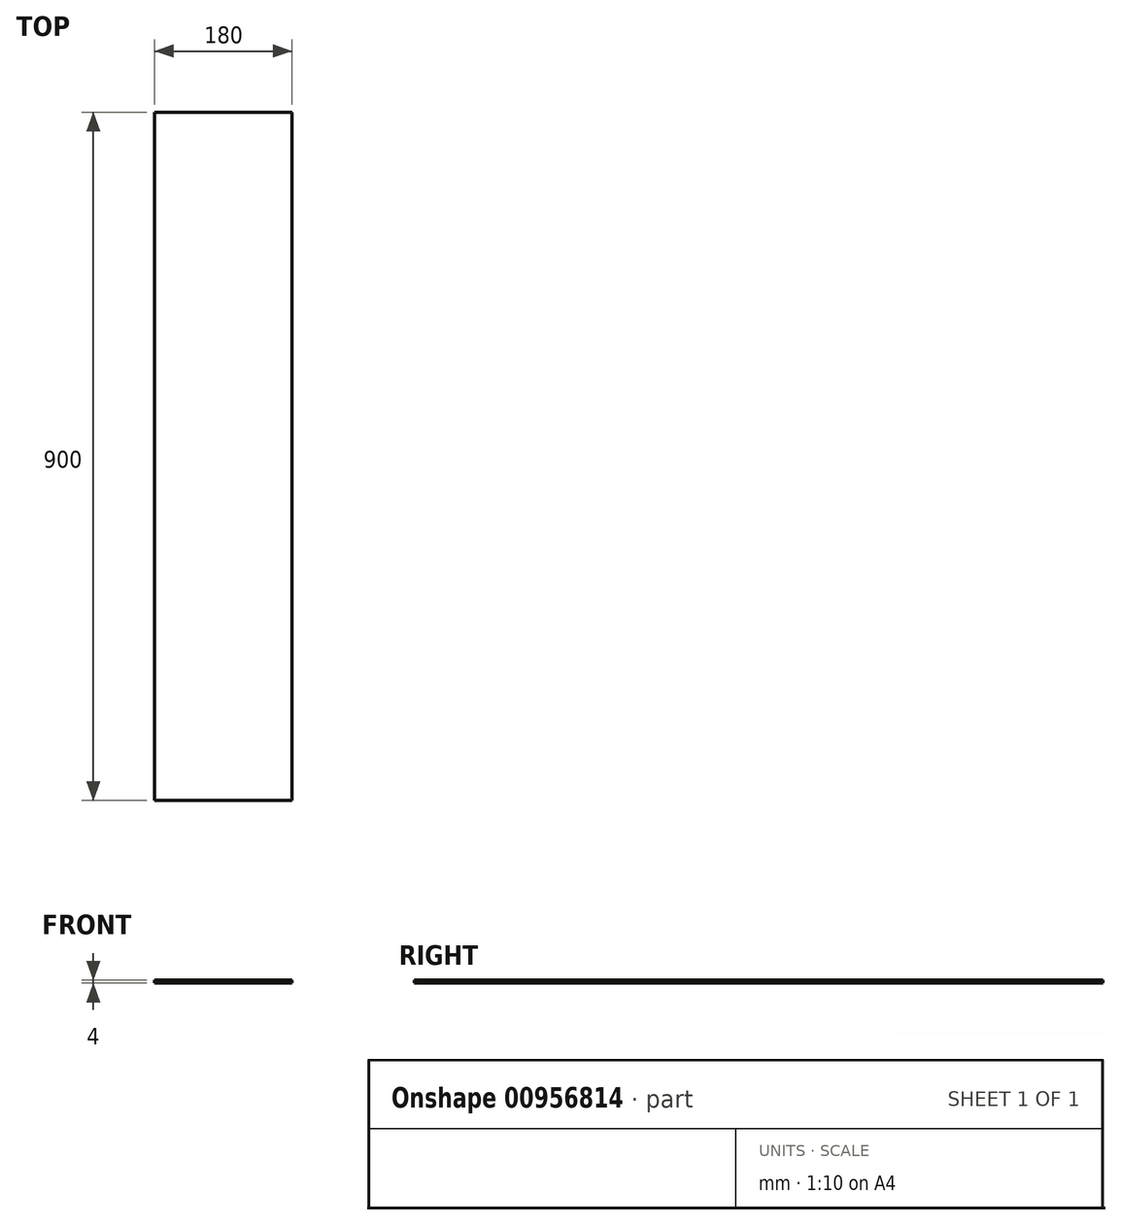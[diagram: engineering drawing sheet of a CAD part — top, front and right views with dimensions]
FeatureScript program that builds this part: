
annotation { "Feature Type Name" : "Feature", "Feature Type Description" : "" }
export const myFeature = defineFeature(function(context is Context, id is Id, definition is map)
    precondition{}
    {
        {
            var Q0;
            Q0=qCreatedBy(makeId("Top.planeOp"),FACE);
            var sketch = newSketch(context, id + "F0", { "sketchPlane" : qUnion([Q0])});
            skLineSegment(sketch, "E0.bottom", {"start": v(90, 450) * mm, "end": v(-90, 450) * mm});
            skLineSegment(sketch, "E0.top", {"start": v(90, -450) * mm, "end": v(-90, -450) * mm});
            skLineSegment(sketch, "E0.left", {"start": v(90, 450) * mm, "end": v(90, -450) * mm});
            skLineSegment(sketch, "E0.right", {"start": v(-90, 450) * mm, "end": v(-90, -450) * mm});
            skPoint(sketch, "E0.middle", {"position": v(0, 0) * mm});
            skSolve(sketch);
        }
        {
            var Q0;
            Q0=qSketchRegion(id+"F0",true);
            extrude(context, id + "F1", {"entities" : qUnion([Q0]), "depth" : 4 * mm, "offsetDistance" : 25 * mm});
        }
    });
